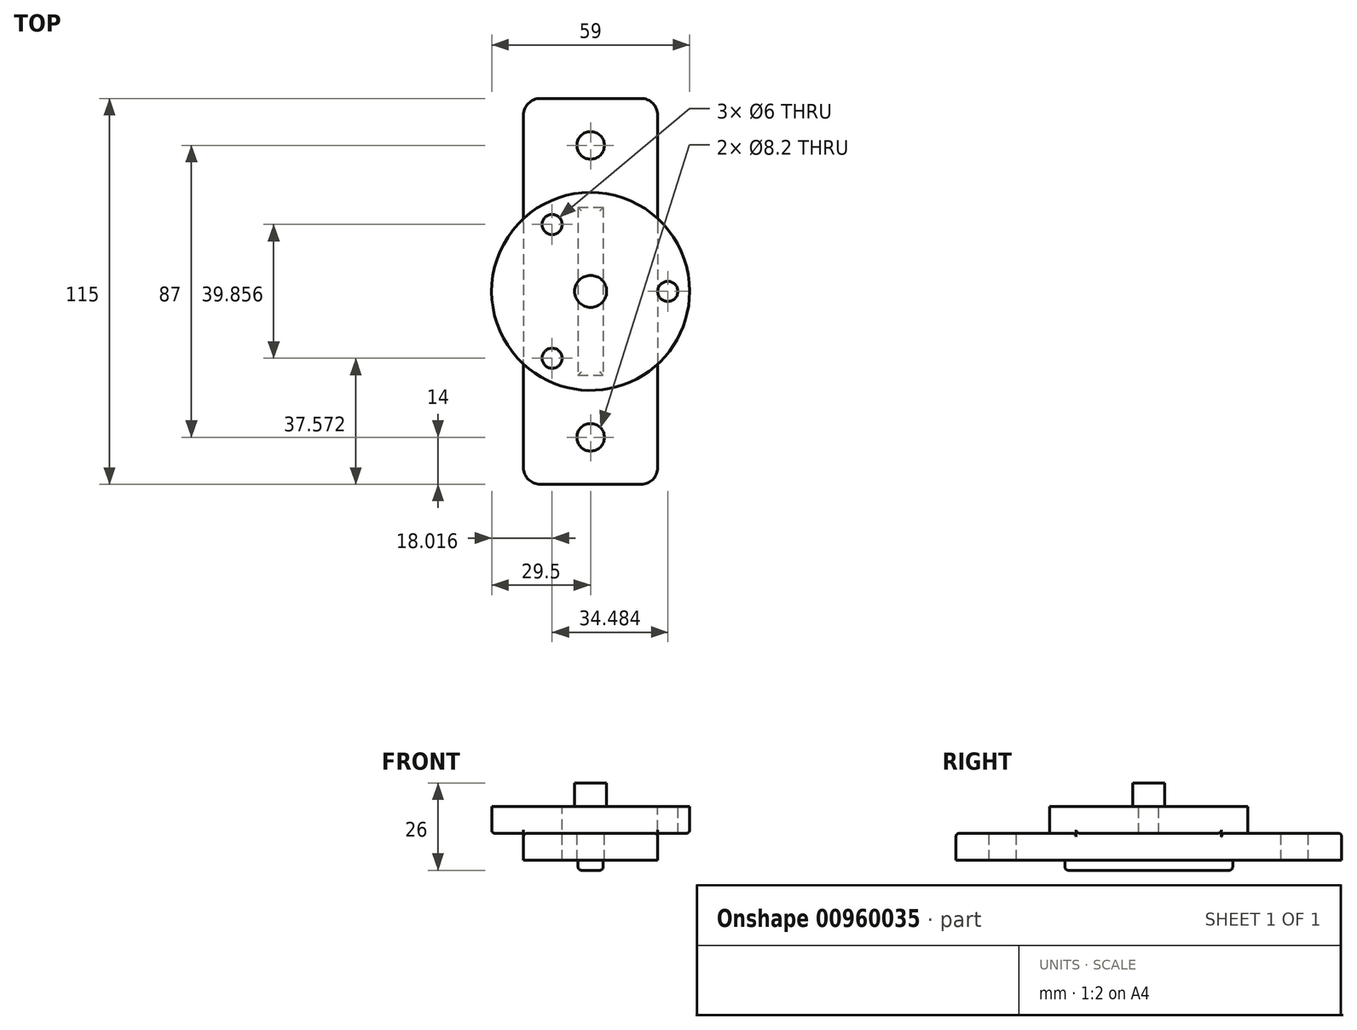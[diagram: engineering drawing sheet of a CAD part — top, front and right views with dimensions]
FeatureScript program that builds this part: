
annotation { "Feature Type Name" : "Feature", "Feature Type Description" : "" }
export const myFeature = defineFeature(function(context is Context, id is Id, definition is map)
    precondition{}
    {
        {
            var Q0;
            Q0=qCreatedBy(makeId("Top.planeOp"),FACE);
            var sketch = newSketch(context, id + "F0", { "sketchPlane" : qUnion([Q0])});
            skLineSegment(sketch, "E0.bottom", {"start": v(20, 57.5) * mm, "end": v(-20, 57.5) * mm});
            skLineSegment(sketch, "E0.top", {"start": v(20, -57.5) * mm, "end": v(-20, -57.5) * mm});
            skLineSegment(sketch, "E0.left", {"start": v(20, 57.5) * mm, "end": v(20, -57.5) * mm});
            skLineSegment(sketch, "E0.right", {"start": v(-20, 57.5) * mm, "end": v(-20, -57.5) * mm});
            skPoint(sketch, "E0.middle", {"position": v(0, 0) * mm});
            skCircle(sketch, "E1", {"center": v(0, 0) * mm, "radius": 29.5 * mm});
            skPoint(sketch, "E2", {"position": v(0, -43.5) * mm});
            skCircle(sketch, "E3", {"center": v(0, -43.5) * mm, "radius": 4.1 * mm});
            skPoint(sketch, "E4", {"position": v(0, 43.5) * mm});
            skCircle(sketch, "E5", {"center": v(0, 43.5) * mm, "radius": 4.1 * mm});
            skPoint(sketch, "E6", {"position": v(0, 47.6) * mm});
            skPoint(sketch, "E7", {"position": v(0, 39.4) * mm});
            skPoint(sketch, "E8", {"position": v(0, -39.4) * mm});
            skPoint(sketch, "E9", {"position": v(0, -47.6) * mm});
            skSolve(sketch);
        }
        {
            var Q0;
            {var subQ5=sQuery(id+"F0.wireOp",EDGE,"E0.bottom");Q0=makeQuery(id+"F0.imprint","IMPRINT",FACE,{"disambiguationData":[TD([[makeQuery(id+"F0.imprint","IMPRINT",EDGE,{"derivedFrom":subQ5}),1.0]])]});}
            var Q1;
            {var subQ5=sQuery(id+"F0.wireOp",EDGE,"E0.top");Q1=makeQuery(id+"F0.imprint","IMPRINT",FACE,{"disambiguationData":[TD([[makeQuery(id+"F0.imprint","IMPRINT",EDGE,{"derivedFrom":subQ5}),-1.0]])]});}
            var Q2;
            {var subQ0=sQuery(id+"F0.wireOp",EDGE,"E1");var subQ1=sQuery(id+"F0.wireOp",EDGE,"E0.left");var subQ2=makeQuery(id+"F0.imprint","INTERSECT",VERTEX,{"disambiguationData":[OD(0.0)],"derivedFrom":[subQ1,subQ0]});Q2=makeQuery(id+"F0.imprint","IMPRINT",FACE,{"disambiguationData":[TD([[makeQuery(id+"F0.imprint","IMPRINT",EDGE,{"disambiguationData":[TD([[subQ2,-1.0]])],"derivedFrom":subQ1}),-1.0]])]});}
            extrude(context, id + "F1", {"entities" : qUnion([Q0, Q1, Q2]), "oppositeDirection" : true, "depth" : 8 * mm, "offsetDistance" : 25 * mm});
        }
        {
            var Q0;
            {var subQ0=sQuery(id+"F0.wireOp",EDGE,"E1");var subQ1=sQuery(id+"F0.wireOp",EDGE,"E0.left");var subQ2=makeQuery(id+"F0.imprint","INTERSECT",VERTEX,{"disambiguationData":[OD(0.0)],"derivedFrom":[subQ1,subQ0]});Q0=makeQuery(id+"F0.imprint","IMPRINT",FACE,{"disambiguationData":[TD([[makeQuery(id+"F0.imprint","IMPRINT",EDGE,{"disambiguationData":[TD([[subQ2,-1.0]])],"derivedFrom":subQ1}),1.0]])]});}
            var Q1;
            {var subQ0=sQuery(id+"F0.wireOp",EDGE,"E1");var subQ1=sQuery(id+"F0.wireOp",EDGE,"E0.right");var subQ2=makeQuery(id+"F0.imprint","INTERSECT",VERTEX,{"disambiguationData":[OD(0.0)],"derivedFrom":[subQ1,subQ0]});Q1=makeQuery(id+"F0.imprint","IMPRINT",FACE,{"disambiguationData":[TD([[makeQuery(id+"F0.imprint","IMPRINT",EDGE,{"disambiguationData":[TD([[subQ2,-1.0]])],"derivedFrom":subQ1}),-1.0]])]});}
            var Q2;
            {var subQ0=sQuery(id+"F0.wireOp",EDGE,"E1");var subQ1=sQuery(id+"F0.wireOp",EDGE,"E0.left");var subQ2=makeQuery(id+"F0.imprint","INTERSECT",VERTEX,{"disambiguationData":[OD(0.0)],"derivedFrom":[subQ1,subQ0]});Q2=makeQuery(id+"F0.imprint","IMPRINT",FACE,{"disambiguationData":[TD([[makeQuery(id+"F0.imprint","IMPRINT",EDGE,{"disambiguationData":[TD([[subQ2,-1.0]])],"derivedFrom":subQ1}),-1.0]])]});}
            extrude(context, id + "F2", {"entities" : qUnion([Q0, Q1, Q2]), "operationType" : NewBodyOperationType.ADD, "depth" : 8 * mm, "offsetDistance" : 25 * mm});
        }
        {
            var Q0;
            Q0=makeQuery(id+"F1.opExtrude","SWEPT_EDGE",EDGE,{"disambiguationData":[OSD([sQuery(id+"F0.wireOp",EDGE,"E0.top"),sQuery(id+"F0.wireOp",EDGE,"E0.right")])]});
            var Q1;
            Q1=makeQuery(id+"F1.opExtrude","SWEPT_EDGE",EDGE,{"disambiguationData":[OSD([sQuery(id+"F0.wireOp",EDGE,"E0.top"),sQuery(id+"F0.wireOp",EDGE,"E0.left")])]});
            var Q2;
            Q2=makeQuery(id+"F1.opExtrude","SWEPT_EDGE",EDGE,{"disambiguationData":[OSD([sQuery(id+"F0.wireOp",EDGE,"E0.bottom"),sQuery(id+"F0.wireOp",EDGE,"E0.right")])]});
            var Q3;
            Q3=makeQuery(id+"F1.opExtrude","SWEPT_EDGE",EDGE,{"disambiguationData":[OSD([sQuery(id+"F0.wireOp",EDGE,"E0.bottom"),sQuery(id+"F0.wireOp",EDGE,"E0.left")])]});
            fillet(context, id + "F3", {"entities" : qUnion([Q0, Q1, Q2, Q3]), "radius" : 5 * mm, "tangentPropagation" : true, "allowEdgeOverflow" : false});
        }
        {
            var Q0;
            {var subQ0=sQuery(id+"F0.wireOp",EDGE,"E0.left");var subQ1=makeQuery(id+"F1.opExtrude","SWEPT_FACE",FACE,{"disambiguationData":[OSD([subQ0])]});var subQ3=sQuery(id+"F0.wireOp",EDGE,"E0.top");var subQ4=makeQuery(id+"F1.opExtrude","CAP_FACE",FACE,{"disambiguationData":[OSD([sQuery(id+"F0.wireOp",EDGE,"E0.bottom"),subQ3,subQ0,sQuery(id+"F0.wireOp",EDGE,"E0.right"),sQuery(id+"F0.wireOp",EDGE,"E3"),sQuery(id+"F0.wireOp",EDGE,"E5")])],"isStart":true});Q0=makeQuery(id+"F2.boolean.opBoolean","SPLIT",EDGE,{"disambiguationData":[topologyDisambiguationEdgeConnected([subQ4,subQ1]),TD([makeQuery(id+"F1.opExtrude","SWEPT_FACE",FACE,{"disambiguationData":[OSD([subQ3])]})])],"derivedFrom":makeQuery(id+"F1.opExtrude","CAP_EDGE",EDGE,{"disambiguationData":[OSD([subQ0])],"isStart":true})});}
            var Q1;
            {var subQ0=sQuery(id+"F0.wireOp",EDGE,"E0.left");var subQ1=makeQuery(id+"F1.opExtrude","SWEPT_FACE",FACE,{"disambiguationData":[OSD([subQ0])]});var subQ3=sQuery(id+"F0.wireOp",EDGE,"E0.bottom");var subQ4=makeQuery(id+"F1.opExtrude","CAP_FACE",FACE,{"disambiguationData":[OSD([subQ3,sQuery(id+"F0.wireOp",EDGE,"E0.top"),subQ0,sQuery(id+"F0.wireOp",EDGE,"E0.right"),sQuery(id+"F0.wireOp",EDGE,"E3"),sQuery(id+"F0.wireOp",EDGE,"E5")])],"isStart":true});Q1=makeQuery(id+"F2.boolean.opBoolean","SPLIT",EDGE,{"disambiguationData":[topologyDisambiguationEdgeConnected([subQ4,subQ1]),TD([makeQuery(id+"F1.opExtrude","SWEPT_FACE",FACE,{"disambiguationData":[OSD([subQ3])]})])],"derivedFrom":makeQuery(id+"F1.opExtrude","CAP_EDGE",EDGE,{"disambiguationData":[OSD([subQ0])],"isStart":true})});}
            fillet(context, id + "F4", {"entities" : qUnion([Q0, Q1]), "radius" : 1 * mm, "tangentPropagation" : true, "allowEdgeOverflow" : false});
        }
        {
            var Q0;
            {var subQ0=sQuery(id+"F0.wireOp",EDGE,"E0.left");var subQ1=sQuery(id+"F0.wireOp",EDGE,"E1");var subQ2=makeQuery(id+"F2.opExtrude","SWEPT_FACE",FACE,{"disambiguationData":[OSD([subQ1])]});var subQ3=makeQuery(id+"F2.opExtrude","CAP_FACE",FACE,{"disambiguationData":[OSD([subQ1])],"isStart":true});Q0=makeQuery(id+"F2.boolean.opBoolean","SPLIT",EDGE,{"disambiguationData":[topologyDisambiguationEdgeConnected([subQ2,subQ3]),TD([makeQuery(id+"F1.opExtrude","SWEPT_FACE",FACE,{"disambiguationData":[OSD([subQ0])]})])],"derivedFrom":makeQuery(id+"F2.opExtrude","CAP_EDGE",EDGE,{"disambiguationData":[OSD([subQ1])],"isStart":true})});}
            var Q1;
            {var subQ0=sQuery(id+"F0.wireOp",EDGE,"E0.right");var subQ1=sQuery(id+"F0.wireOp",EDGE,"E1");var subQ2=makeQuery(id+"F2.opExtrude","SWEPT_FACE",FACE,{"disambiguationData":[OSD([subQ1])]});var subQ3=makeQuery(id+"F2.opExtrude","CAP_FACE",FACE,{"disambiguationData":[OSD([subQ1])],"isStart":true});Q1=makeQuery(id+"F2.boolean.opBoolean","SPLIT",EDGE,{"disambiguationData":[topologyDisambiguationEdgeConnected([subQ2,subQ3]),TD([makeQuery(id+"F1.opExtrude","SWEPT_FACE",FACE,{"disambiguationData":[OSD([subQ0])]})])],"derivedFrom":makeQuery(id+"F2.opExtrude","CAP_EDGE",EDGE,{"disambiguationData":[OSD([subQ1])],"isStart":true})});}
            fillet(context, id + "F5", {"entities" : qUnion([Q0, Q1]), "radius" : 1 * mm, "tangentPropagation" : true, "allowEdgeOverflow" : false});
        }
        {
            var Q0;
            Q0=makeQuery(id+"F2.opExtrude","CAP_FACE",FACE,{"disambiguationData":[OSD([sQuery(id+"F0.wireOp",EDGE,"E1")])],"isStart":false});
            var sketch = newSketch(context, id + "F6", { "sketchPlane" : qUnion([Q0])});
            skPoint(sketch, "E10", {"position": v(23, 0) * mm});
            skPoint(sketch, "E11", {"position": v(-11.48, -19.93) * mm});
            skPoint(sketch, "E12", {"position": v(-11.48, 19.93) * mm});
            skCircle(sketch, "E13", {"center": v(-11.48, -19.93) * mm, "radius": 3 * mm});
            skCircle(sketch, "E14", {"center": v(23, 0) * mm, "radius": 3 * mm});
            skCircle(sketch, "E15", {"center": v(-11.48, 19.93) * mm, "radius": 3 * mm});
            skCircle(sketch, "E16", {"center": v(0, 0) * mm, "radius": 4.76 * mm});
            skSolve(sketch);
        }
        {
            var Q0;
            Q0=makeQuery(id+"F1.opExtrude","CAP_FACE",FACE,{"disambiguationData":[OSD([sQuery(id+"F0.wireOp",EDGE,"E0.bottom"),sQuery(id+"F0.wireOp",EDGE,"E0.top"),sQuery(id+"F0.wireOp",EDGE,"E0.left"),sQuery(id+"F0.wireOp",EDGE,"E0.right"),sQuery(id+"F0.wireOp",EDGE,"E3"),sQuery(id+"F0.wireOp",EDGE,"E5")])],"isStart":false});
            var sketch = newSketch(context, id + "F7", { "sketchPlane" : qUnion([Q0])});
            skLineSegment(sketch, "E17.bottom", {"start": v(-3.75, -25) * mm, "end": v(3.75, -25) * mm});
            skLineSegment(sketch, "E17.top", {"start": v(-3.75, 25) * mm, "end": v(3.75, 25) * mm});
            skLineSegment(sketch, "E17.left", {"start": v(-3.75, -25) * mm, "end": v(-3.75, 25) * mm});
            skLineSegment(sketch, "E17.right", {"start": v(3.75, -25) * mm, "end": v(3.75, 25) * mm});
            skPoint(sketch, "E17.middle", {"position": v(0, 0) * mm});
            skSolve(sketch);
        }
        {
            var Q0;
            Q0=qSketchRegion(id+"F7",true);
            extrude(context, id + "F8", {"entities" : qUnion([Q0]), "operationType" : NewBodyOperationType.ADD, "depth" : 3 * mm, "offsetDistance" : 25 * mm});
        }
        {
            var Q0;
            Q0=makeQuery(id+"F8.opExtrude","CAP_EDGE",EDGE,{"disambiguationData":[OSD([sQuery(id+"F7.wireOp",EDGE,"E17.bottom")])],"isStart":false});
            var Q1;
            Q1=makeQuery(id+"F8.opExtrude","CAP_EDGE",EDGE,{"disambiguationData":[OSD([sQuery(id+"F7.wireOp",EDGE,"E17.right")])],"isStart":false});
            var Q2;
            Q2=makeQuery(id+"F8.opExtrude","CAP_EDGE",EDGE,{"disambiguationData":[OSD([sQuery(id+"F7.wireOp",EDGE,"E17.left")])],"isStart":false});
            var Q3;
            Q3=makeQuery(id+"F8.opExtrude","CAP_EDGE",EDGE,{"disambiguationData":[OSD([sQuery(id+"F7.wireOp",EDGE,"E17.top")])],"isStart":false});
            fillet(context, id + "F9", {"entities" : qUnion([Q0, Q1, Q2, Q3]), "radius" : 1 * mm, "tangentPropagation" : true, "allowEdgeOverflow" : false});
        }
        {
            var Q0;
            Q0=makeQuery(id+"F6.imprint","IMPRINT",FACE,{"disambiguationData":[TD([[makeQuery(id+"F6.imprint","IMPRINT",EDGE,{"derivedFrom":sQuery(id+"F6.wireOp",EDGE,"E13")}),1.0]])]});
            var Q1;
            Q1=makeQuery(id+"F6.imprint","IMPRINT",FACE,{"disambiguationData":[TD([[makeQuery(id+"F6.imprint","IMPRINT",EDGE,{"derivedFrom":sQuery(id+"F6.wireOp",EDGE,"E15")}),1.0]])]});
            var Q2;
            Q2=makeQuery(id+"F6.imprint","IMPRINT",FACE,{"disambiguationData":[TD([[makeQuery(id+"F6.imprint","IMPRINT",EDGE,{"derivedFrom":sQuery(id+"F6.wireOp",EDGE,"E14")}),1.0]])]});
            extrude(context, id + "F10", {"entities" : qUnion([Q0, Q1, Q2]), "operationType" : NewBodyOperationType.REMOVE, "oppositeDirection" : true, "depth" : 25 * mm, "offsetDistance" : 25 * mm});
        }
        {
            var Q0;
            Q0=makeQuery(id+"F6.imprint","IMPRINT",FACE,{"disambiguationData":[TD([[makeQuery(id+"F6.imprint","IMPRINT",EDGE,{"derivedFrom":sQuery(id+"F6.wireOp",EDGE,"E16")}),1.0]])]});
            extrude(context, id + "F11", {"entities" : qUnion([Q0]), "operationType" : NewBodyOperationType.ADD, "depth" : 7 * mm, "offsetDistance" : 25 * mm});
        }
    });
